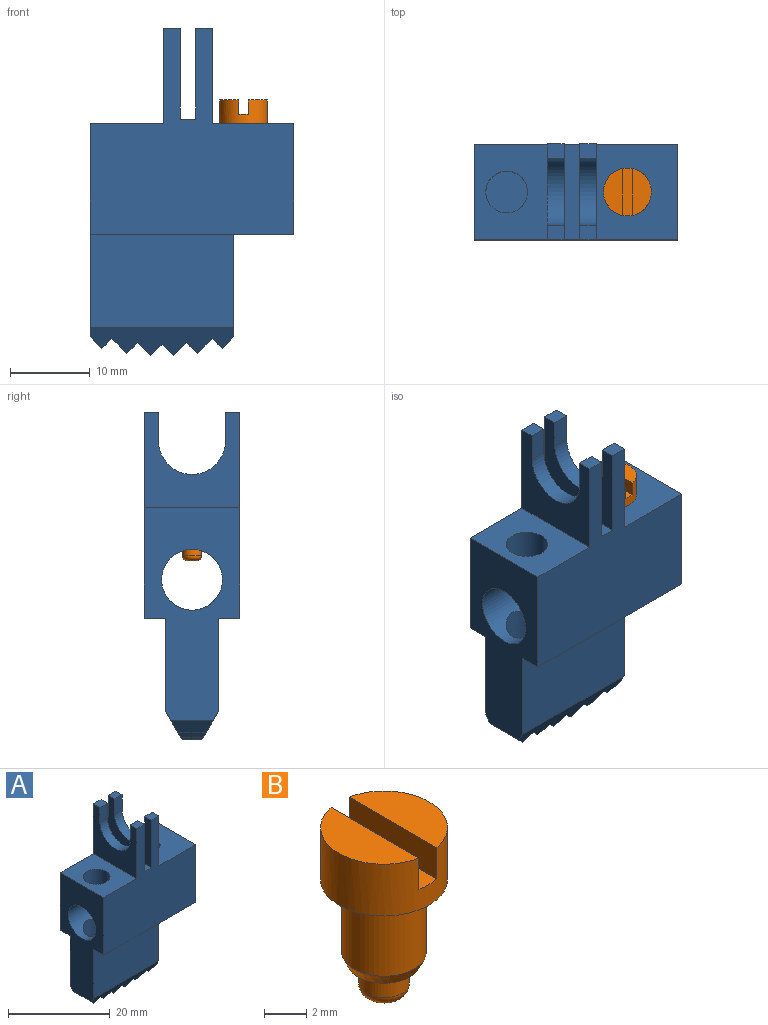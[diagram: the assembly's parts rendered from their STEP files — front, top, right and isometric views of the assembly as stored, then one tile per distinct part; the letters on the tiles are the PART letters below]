
ASSEMBLY  parts=2 mates=1
PART A: 44 faces, bbox 25.5x12x41.1 mm
  f0: plane 12.89x6.6mm, normal (1,0,0), area 84.3mm2, adj f7,f17,f18,f30,f31,f39
  f1: plane 2.1x1.8mm, normal (0,0,1), area 3.8mm2, adj f3,f10,f15,f22
  f2: plane 2.1x1.8mm, normal (0,0,1), area 3.8mm2, adj f3,f10,f16,f23
  f3: plane 12x11.4mm, normal (-1,0,0), area 78.9mm2, adj f1,f2,f11,f15,f16,f22,f23,f24
  f4: plane 12x11.4mm, normal (1,0,0), area 78.9mm2, adj f5,f6,f11,f15,f16,f19,f20,f21
  f5: plane 2.1x1.8mm, normal (0,0,1), area 3.8mm2, adj f4,f12,f15,f21
  f6: plane 2.1x1.8mm, normal (0,0,1), area 3.8mm2, adj f4,f12,f16,f20
  f7: plane 25.5x12mm, normal (0,0,-1), area 187.2mm2, adj f0,f8,f14,f15,f16,f17,f18
  f8: plane 13.8x12mm, normal (1,0,0), area 119.9mm2, adj f7,f9,f15,f16,f25
  f9: plane 12x10.2mm, normal (0,0,1), area 112.8mm2, adj f8,f10,f15,f16,f26
  f10: plane 12x12mm, normal (1,0,0), area 86.1mm2, adj f1,f2,f9,f15,f16,f22,f23,f24
  f11: plane 12x1.94mm, normal (0,0,1), area 23.3mm2, adj f3,f4,f15,f16
  f12: plane 12x12mm, normal (-1,0,0), area 86.1mm2, adj f5,f6,f13,f15,f16,f19,f20,f21
  f13: plane 12x9.16mm, normal (0,0,1), area 88.4mm2, adj f12,f14,f15,f16,f27
  f14: plane 26.69x12mm, normal (-1,0,0), area 204.2mm2, adj f7,f13,f15,f16,f17,f18,f25,f30
  f15: plane 25.8x25.5mm, normal (0,-1,0), area 403.5mm2, adj f1,f3,f4,f5,f7,f8,f9,f10
  f16: plane 25.8x25.5mm, normal (0,1,0), area 403.5mm2, adj f2,f3,f4,f6,f7,f8,f9,f10
  f17: plane 18x11.7mm, normal (0,-1,0), area 210.6mm2, adj f0,f7,f14,f31
  f18: plane 18x11.7mm, normal (0,1,0), area 210.6mm2, adj f0,f7,f14,f30
  f19: cylinder r=4.2mm len=8.4mm, axis (1,0,0), area 27.7mm2, adj f4,f12,f20,f21
  f20: plane 3.6x2.1mm, normal (0,-1,0), area 7.6mm2, adj f4,f6,f12,f19
  f21: plane 3.6x2.1mm, normal (0,1,0), area 7.6mm2, adj f4,f5,f12,f19
  f22: plane 3.6x2.1mm, normal (0,1,0), area 7.6mm2, adj f1,f3,f10,f24
  f23: plane 3.6x2.1mm, normal (0,-1,0), area 7.6mm2, adj f2,f3,f10,f24
  f24: cylinder r=4.2mm len=8.4mm, axis (1,0,0), area 27.7mm2, adj f3,f10,f22,f23
  f25: cylinder r=3.81mm len=25.5mm, axis (1,0,0), area 554.9mm2, adj f8,f14,f26,f27,f28
  f26: cylinder r=1.75mm len=5.61mm, axis (0,0,1), area 59.3mm2, adj f9,f25
  f27: cylinder r=2.62mm len=6.23mm, axis (0,0,1), area 93.6mm2, adj f13,f25
  f28: cylinder r=2.62mm len=11.33mm, axis (0,0,1), area 177.5mm2, adj f25,f29
  f29: plane 5.24x5.24mm, normal (0,0,1), area 21.5mm2, adj f28
  f30: plane 18x3.56mm, normal (0,0.87,-0.5), area 50.2mm2, adj f0,f14,f18,f32,f33,f34,f35,f36
  f31: plane 18x3.56mm, normal (0,-0.87,-0.5), area 50.2mm2, adj f0,f14,f17,f32,f33,f34,f35,f36
  f32: plane 4.18x1.46mm, normal (-0.71,0,-0.71), area 6.9mm2, adj f30,f31,f33,f43
  f33: plane 4.18x1.46mm, normal (0.71,0,-0.71), area 6.9mm2, adj f30,f31,f32,f34
  f34: plane 4.37x1.63mm, normal (-0.71,0,-0.71), area 7.9mm2, adj f30,f31,f33,f35
  f35: plane 4.37x1.34mm, normal (0.71,0,-0.71), area 6.8mm2, adj f30,f31,f34,f36
  f36: plane 4.99x1.88mm, normal (-0.71,0,-0.71), area 10.4mm2, adj f30,f31,f35,f37
  f37: plane 4.99x1.24mm, normal (0.71,0,-0.71), area 7.5mm2, adj f30,f31,f36,f38
  f38: plane 5.23x1.44mm, normal (-0.71,0,-0.71), area 9mm2, adj f14,f30,f31,f37
  f39: plane 5.23x1.44mm, normal (0.71,0,-0.71), area 9mm2, adj f0,f30,f31,f40
  f40: plane 4.99x1.24mm, normal (-0.71,0,-0.71), area 7.5mm2, adj f30,f31,f39,f41
  f41: plane 4.99x1.88mm, normal (0.71,0,-0.71), area 10.4mm2, adj f30,f31,f40,f42
  f42: plane 4.37x1.34mm, normal (-0.71,0,-0.71), area 6.8mm2, adj f30,f31,f41,f43
  f43: plane 4.37x1.63mm, normal (0.71,0,-0.71), area 7.9mm2, adj f30,f31,f32,f42
PART B: 13 faces, bbox 6x6x9.6 mm
  f0: plane 5.88x2.4mm, normal (0,0,1), area 10.6mm2, adj f9,f10
  f1: plane 5.88x2.4mm, normal (0,0,1), area 10.6mm2, adj f9,f11
  f2: plane 1.2x1.2mm, normal (0,0,-1), area 1.1mm2, adj f3
  f3: torus R=0.6mm, axis (0,0,1), area 5.8mm2, adj f2,f4
  f4: cylinder r=1.2mm len=2.4mm, axis (0,0,1), area 9mm2, adj f3,f5
  f5: plane 3.44x3.44mm, normal (0,0,-1), area 4.8mm2, adj f4,f6
  f6: cone r=1.72mm half-angle=25deg, axis (0,0,1), area 7.7mm2, adj f5,f7
  f7: cylinder r=2mm len=4.2mm, axis (0,0,1), area 52.8mm2, adj f6,f8
  f8: plane 6x6mm, normal (0,0,-1), area 15.7mm2, adj f7,f9
  f9: cylinder r=3mm len=6mm, axis (0,0,1), area 52.2mm2, adj f0,f1,f8,f10,f11,f12
  f10: plane 5.88x1.8mm, normal (1,0,0), area 10.6mm2, adj f0,f9,f12
  f11: plane 5.88x1.8mm, normal (-1,0,0), area 10.6mm2, adj f1,f9,f12
  f12: plane 6x1.2mm, normal (0,0,1), area 7.2mm2, adj f9,f10,f11
PLACE A t=(-0.8,-2.5,-19.4)mm
PLACE B t=(0.4,-2.5,3.1)mm
MATE fastened B.f3 <-> A.f26  axis (0,0,1) through (0.4,-2.5,9.7)mm
